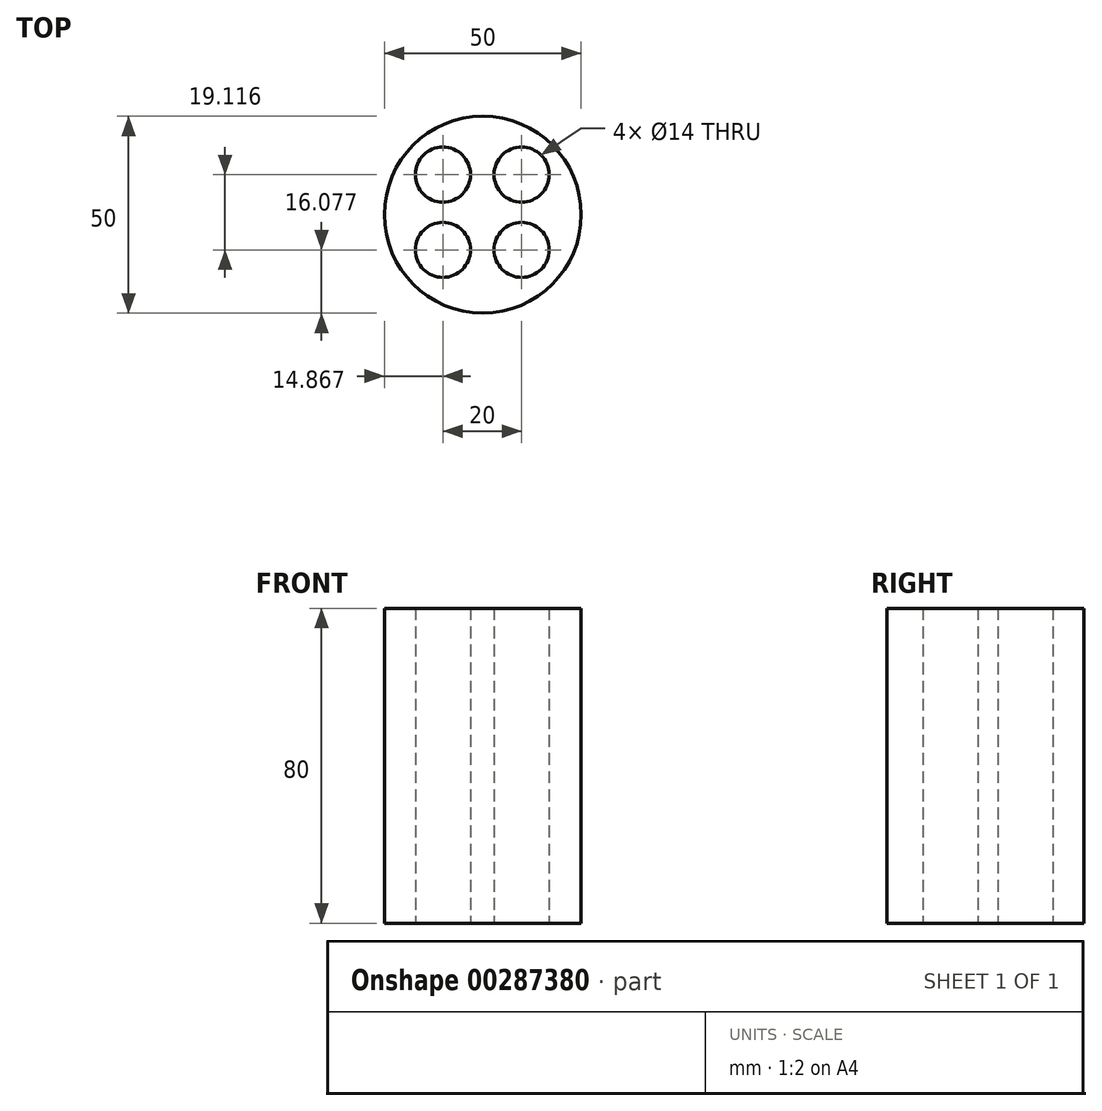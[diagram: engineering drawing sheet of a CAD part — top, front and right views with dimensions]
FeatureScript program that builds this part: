
annotation { "Feature Type Name" : "Feature", "Feature Type Description" : "" }
export const myFeature = defineFeature(function(context is Context, id is Id, definition is map)
    precondition{}
    {
        {
            var Q0;
            Q0=qCreatedBy(makeId("Top.planeOp"),FACE);
            var sketch = newSketch(context, id + "F0", { "sketchPlane" : qUnion([Q0])});
            skCircle(sketch, "E0", {"center": v(0, 0) * mm, "radius": 25 * mm});
            skCircle(sketch, "E1", {"center": v(-10.13, 10.2) * mm, "radius": 7 * mm});
            skCircle(sketch, "E2", {"center": v(9.87, 10.2) * mm, "radius": 7 * mm});
            skCircle(sketch, "E3", {"center": v(-10.13, -8.92) * mm, "radius": 7 * mm});
            skCircle(sketch, "E4", {"center": v(9.87, -8.92) * mm, "radius": 7 * mm});
            skSolve(sketch);
        }
        {
            var Q0;
            Q0 = qSketchRegion(id + "F0", true);
            extrude(context, id + "F1", {"entities" : qUnion([Q0]), "depth" : 80 * mm});
        }
    });
